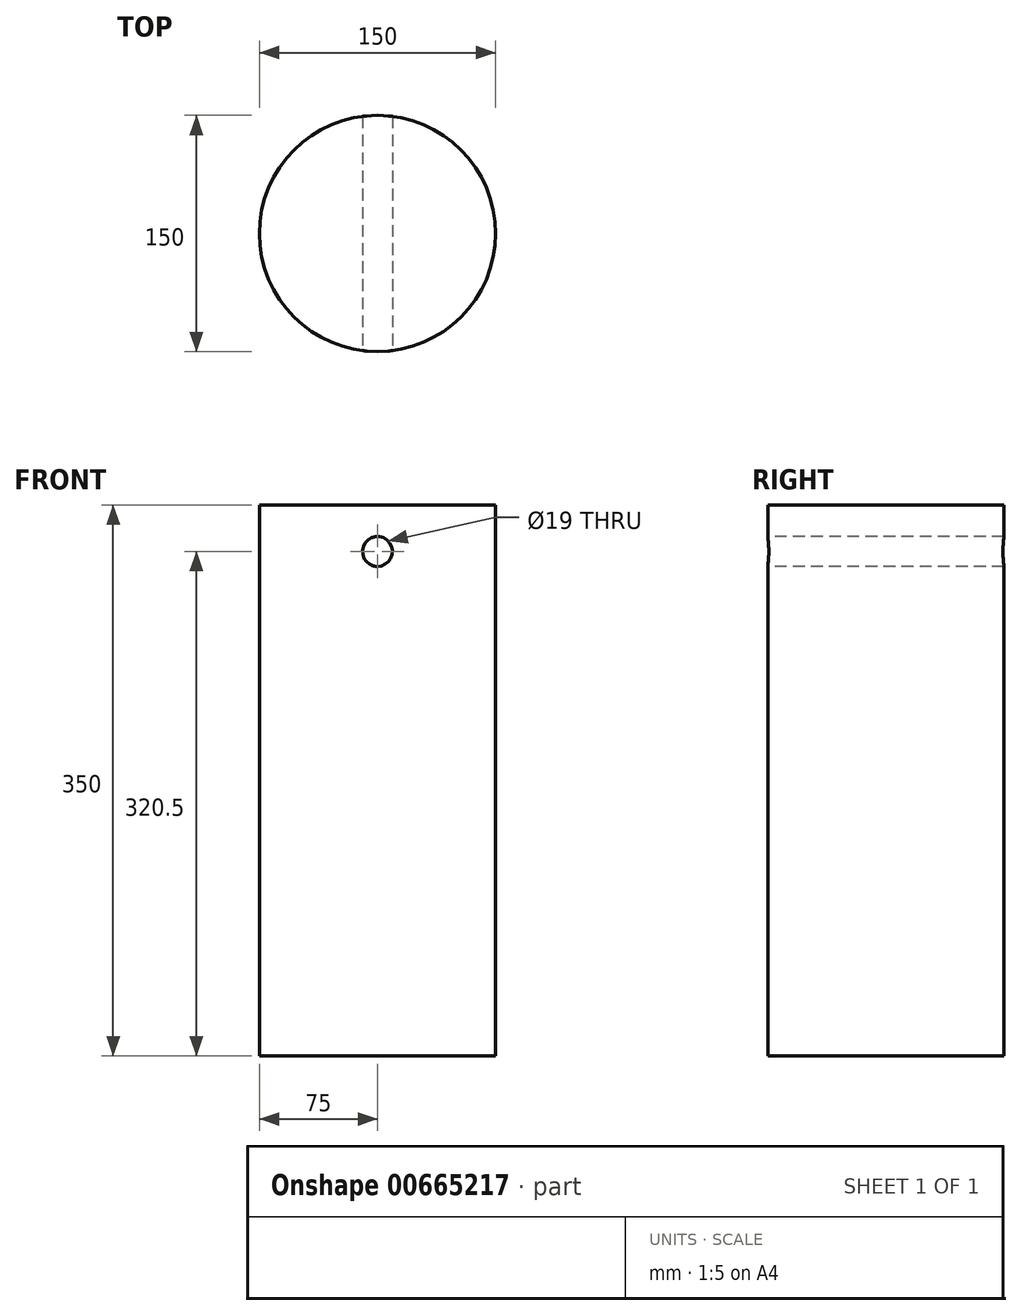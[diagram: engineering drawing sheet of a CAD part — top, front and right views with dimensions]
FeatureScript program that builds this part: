
annotation { "Feature Type Name" : "Feature", "Feature Type Description" : "" }
export const myFeature = defineFeature(function(context is Context, id is Id, definition is map)
    precondition{}
    {
        {
            var Q0;
            Q0=qCreatedBy(makeId("Top.planeOp"),FACE);
            var sketch = newSketch(context, id + "F0", { "sketchPlane" : qUnion([Q0])});
            skCircle(sketch, "E0", {"center": v(0, 0) * mm, "radius": 75 * mm});
            skSolve(sketch);
        }
        {
            var Q0;
            Q0=makeQuery(id+"F0.imprint","IMPRINT",FACE,{"disambiguationData":[TD([[makeQuery(id+"F0.imprint","IMPRINT",EDGE,{"derivedFrom":sQuery(id+"F0.wireOp",EDGE,"E0")}),1.0]])]});
            extrude(context, id + "F1", {"entities" : qUnion([Q0]), "depth" : 350 * mm, "offsetDistance" : 25 * mm});
        }
        {
            var Q0;
            Q0=qCreatedBy(makeId("Front.planeOp"),FACE);
            var sketch = newSketch(context, id + "F2", { "sketchPlane" : qUnion([Q0])});
            skCircle(sketch, "E1", {"center": v(0, 320.5) * mm, "radius": 9.5 * mm});
            skPoint(sketch, "E2.center.orphan", {"position": v(0, 135.1) * mm});
            skSolve(sketch);
        }
        {
            var Q0;
            Q0 = qSketchRegion(id + "F2", true);
            extrude(context, id + "F3", {"entities" : qUnion([Q0]), "operationType" : NewBodyOperationType.REMOVE, "endBound" : BoundingType.SYMMETRIC, "oppositeDirection" : true, "depth" : 234 * mm, "offsetDistance" : 25 * mm});
        }
    });
